# Revit family: EBRE-LED-236x-OSDx
name_source: partatom
category: Oprawy oświetleniowe
units: mm (PartAtom-declared; Revit-internal decimal feet)

## family parameters
Numer OmniClass = 23.80.70.11
Obiekt nadrzędny = Powierzchnia
Punkt obliczania pomieszczeń = Nie
Tnij formami wycięć po wczytaniu = Nie
Typ części = Normalny
Tytuł OmniClass = Luminaries for Internal Lighting
Współdzielony = Nie
Wymiar okrągłego złącza = Użyj średnicy
Źródło światła = Tak

## types (8) — shared parameters
Emituj kształt widoczny w renderingu = Nie
Emituj z długości prostokąta = 224 mm  [stored 0.734908 ft]
Emituj z szerokości prostokąta = 1184 mm  [stored 3.88451 ft]
Filtr koloru = 16777215
Kod zespołu = D5020200
Lampa = LED
Odchylenie kierunku = 90.00°
Plik sieci fotometrycznej = EBRE-LED 2365200840 OSD.IES
Producent = RIDI Leuchten GmbH
URL = www.ridi.de
Zmiana temperatury barwowej przyciemniania lampy = <Brak>
brand = RIDI
conformity mark = CE
electrical safety class = 1
height = 90 mm  [stored 0.295276 ft]
ingress protection (IP) code = IP54
length = 1247 mm  [stored 4.09121 ft]
nominal frequency = 50-60Hz
nominal voltage = 230
voltage type (AC, DC, UC) = AC
weight = 9kg
width = 310 mm  [stored 1.01706 ft]
zero-valued in all types: Domyślna rzędna

## per-type parameters (varying)
| type | Model | Obciążenie pozorne | rated input power |
| EBRE-LED 236/2500-830 OSD | 0822856 | 16 VA | 16 |
| EBRE-LED 236/2500-830 OSD-DA | 0832856 | 16 VA | 16 |
| EBRE-LED 236/2700-840 OSD | 0822840 | 16 VA | 16 |
| EBRE-LED 236/2700-840 OSD-DA | 0832840 | 16 VA | 16 |
| EBRE-LED 236/5000-830 OSD | 0822852 | 32 VA | 32 |
| EBRE-LED 236/5200-840 OSD | 0822818 | 32 VA | 32 |
| EBRE-LED 236/5200-840 OSD-DA | 0832818 | 32 VA | 32 |
| EBRE-LED 236/5000-830 OSD-DA | 0832852 | 32 VA | 32 |

note: column(s) folded — value = type name in every type: product name

note: [stored X ft] marks values corroborated as IEEE doubles in the binary element streams (Revit-internal decimal feet)
